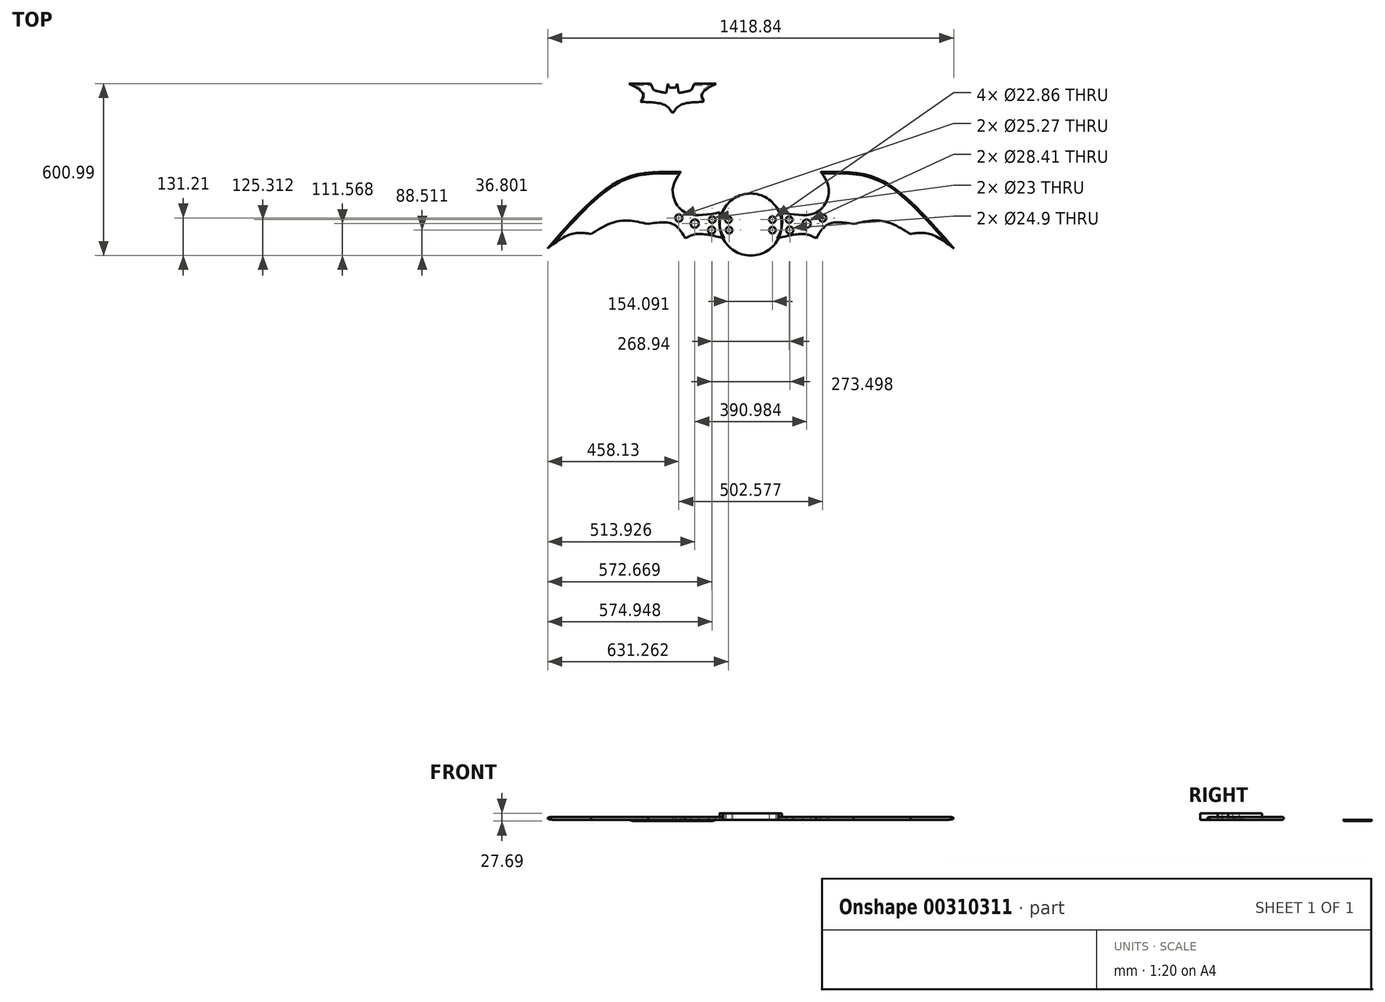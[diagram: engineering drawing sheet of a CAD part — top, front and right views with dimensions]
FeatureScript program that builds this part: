
annotation { "Feature Type Name" : "Feature", "Feature Type Description" : "" }
export const myFeature = defineFeature(function(context is Context, id is Id, definition is map)
    precondition{}
    {
        {
            var Q0;
            Q0=qCreatedBy(makeId("Top.planeOp"),FACE);
            var sketch = newSketch(context, id + "F0", { "sketchPlane" : qUnion([Q0])});
            skLineSegment(sketch, "E0", {"start": v(76.2, 30.48) * mm, "end": v(152.4, 30.48) * mm});
            skLineSegment(sketch, "E1", {"start": v(-76.54, 30.48) * mm, "end": v(-152.74, 30.48) * mm});
            skLineSegment(sketch, "E2", {"start": v(76.2, 30.48) * mm, "end": v(66.04, 7.62) * mm});
            skLineSegment(sketch, "E3", {"start": v(-76.54, 30.48) * mm, "end": v(-66.04, 7.62) * mm});
            skArc(sketch, "E4", {"start": v(-66.04, 7.62) * mm, "mid": v(0, -3.16) * mm, "end": v(66.04, 7.62) * mm});
            skLineSegment(sketch, "E5", {"start": v(21.6, -2.04) * mm, "end": v(16.51, 29.5) * mm});
            skLineSegment(sketch, "E6", {"start": v(16.51, 29.5) * mm, "end": v(11.43, 16.54) * mm});
            skLineSegment(sketch, "E7", {"start": v(11.43, 16.54) * mm, "end": v(-11.43, 16.54) * mm});
            skLineSegment(sketch, "E8", {"start": v(-11.43, 16.54) * mm, "end": v(-16.51, 29.5) * mm});
            skLineSegment(sketch, "E9", {"start": v(-16.51, 29.5) * mm, "end": v(-21.6, -2.04) * mm});
            skPoint(sketch, "E10", {"position": v(0, -76.19) * mm});
            skPoint(sketch, "E11", {"position": v(111.76, -33.5) * mm});
            skPoint(sketch, "E12", {"position": v(-112.1, -33.5) * mm});
            skPoint(sketch, "E13", {"position": v(103.12, -6.18) * mm});
            skPoint(sketch, "E14", {"position": v(-103.47, -6.18) * mm});
            skFitSpline(sketch, "E15", {"points": [v(152.4, 30.48) * mm, v(103.12, -6.18) * mm, v(111.76, -33.5) * mm], "startDerivative": vector(-113.89, -60.03) * mm, "endDerivative": vector(42.43, -68.44) * mm});
            skFitSpline(sketch, "E16", {"points": [v(-152.74, 30.48) * mm, v(-103.47, -6.18) * mm, v(-112.1, -33.5) * mm], "startDerivative": vector(113.89, -60.03) * mm, "endDerivative": vector(-42.43, -68.44) * mm});
            skPoint(sketch, "E17", {"position": v(25.4, -45.7) * mm});
            skPoint(sketch, "E18", {"position": v(-25.4, -45.7) * mm});
            skFitSpline(sketch, "E19", {"points": [v(111.76, -33.5) * mm, v(25.4, -45.7) * mm, v(0, -76.19) * mm], "startDerivative": vector(-168.96, -3.97) * mm, "endDerivative": vector(-46.64, -86.8) * mm});
            skFitSpline(sketch, "E20", {"points": [v(0, -76.19) * mm, v(-25.4, -45.7) * mm, v(-112.1, -33.5) * mm], "startDerivative": vector(-46.65, 86.89) * mm, "endDerivative": vector(-169.55, 3.91) * mm});
            skCircle(sketch, "E21", {"center": v(267.45, 43.06) * mm, "radius": 55.12 * mm});
            skCircle(sketch, "E22", {"center": v(267.45, 43.06) * mm, "radius": 18.05 * mm});
            skPoint(sketch, "E23", {"position": v(238.66, 34.65) * mm});
            skSolve(sketch);
        }
        {
            var Q0;
            {var subQ0=sQuery(id+"F0.wireOp",EDGE,"E5");Q0=makeQuery(id+"F0.imprint","IMPRINT",FACE,{"disambiguationData":[TD([[makeQuery(id+"F0.imprint","IMPRINT",EDGE,{"derivedFrom":subQ0}),1.0]])]});}
            var Q1;
            Q1=makeQuery(id+"F0.imprint","IMPRINT",FACE,{"disambiguationData":[TD([[makeQuery(id+"F0.imprint","IMPRINT",EDGE,{"derivedFrom":sQuery(id+"F0.wireOp",EDGE,"E0")}),-1.0]])]});
            extrude(context, id + "F1", {"entities" : qUnion([Q0, Q1]), "depth" : 4.83 * mm});
        }
        {
            var Q0;
            Q0=makeQuery(id+"F1.opExtrude","CAP_EDGE",EDGE,{"disambiguationData":[OSD([sQuery(id+"F0.wireOp",EDGE,"E0")])],"isStart":true});
            var Q1;
            Q1=makeQuery(id+"F1.opExtrude","CAP_EDGE",EDGE,{"disambiguationData":[OSD([sQuery(id+"F0.wireOp",EDGE,"E1")])],"isStart":true});
            chamfer(context, id + "F2", {"entities" : qUnion([Q0, Q1]), "width" : 5.08 * mm, "tangentPropagation" : true});
        }
        {
            var Q0;
            Q0=makeQuery(id+"F4cRak0Dj6b8y78_0.opExtrude","CAP_EDGE",EDGE,{"disambiguationData":[OSD([sQuery(id+"F0.wireOp",EDGE,"E15")])],"isStart":false});
            var Q1;
            Q1=makeQuery(id+"F1.opExtrude","CAP_EDGE",EDGE,{"disambiguationData":[OSD([sQuery(id+"F0.wireOp",EDGE,"E15")])],"isStart":true});
            var Q2;
            Q2=makeQuery(id+"F1.opExtrude","CAP_EDGE",EDGE,{"disambiguationData":[OSD([sQuery(id+"F0.wireOp",EDGE,"E16")])],"isStart":true});
            var Q3;
            Q3=makeQuery(id+"F1.opExtrude","CAP_EDGE",EDGE,{"disambiguationData":[OSD([sQuery(id+"F0.wireOp",EDGE,"E20")])],"isStart":true});
            fillet(context, id + "F3", {"entities" : qUnion([Q0, Q1, Q2, Q3]), "radius" : 5.08 * mm, "tangentPropagation" : true, "allowEdgeOverflow" : false});
        }
        {
            var Q0;
            Q0=makeQuery(id+"F1.opExtrude","CAP_EDGE",EDGE,{"disambiguationData":[OSD([sQuery(id+"F0.wireOp",EDGE,"E19")])],"isStart":true});
            fillet(context, id + "F4", {"entities" : qUnion([Q0]), "radius" : 5.08 * mm, "tangentPropagation" : true, "allowEdgeOverflow" : false});
        }
        {
            var Q0;
            Q0=makeQuery(id+"F1.opExtrude","CAP_FACE",FACE,{"disambiguationData":[OSD([sQuery(id+"F0.wireOp",EDGE,"E0"),sQuery(id+"F0.wireOp",EDGE,"E1"),sQuery(id+"F0.wireOp",EDGE,"E2"),sQuery(id+"F0.wireOp",EDGE,"E3"),sQuery(id+"F0.wireOp",EDGE,"E4"),sQuery(id+"F0.wireOp",EDGE,"E5"),sQuery(id+"F0.wireOp",EDGE,"E6"),sQuery(id+"F0.wireOp",EDGE,"E7"),sQuery(id+"F0.wireOp",EDGE,"E8"),sQuery(id+"F0.wireOp",EDGE,"E9"),sQuery(id+"F0.wireOp",EDGE,"E15"),sQuery(id+"F0.wireOp",EDGE,"E16"),sQuery(id+"F0.wireOp",EDGE,"E19"),sQuery(id+"F0.wireOp",EDGE,"E20")])],"isStart":false});
            var sketch = newSketch(context, id + "F5", { "sketchPlane" : qUnion([Q0])});
            skPoint(sketch, "E24", {"position": v(165, -419.94) * mm});
            skPoint(sketch, "E25", {"position": v(40.8, -418.85) * mm});
            skPoint(sketch, "E26", {"position": v(-436.54, -545.29) * mm});
            skPoint(sketch, "E27", {"position": v(-288.46, -294.67) * mm});
            skPoint(sketch, "E28", {"position": v(-285.43, -495.15) * mm});
            skPoint(sketch, "E29", {"position": v(-85.93, -460.4) * mm});
            skPoint(sketch, "E30", {"position": v(0, -460.4) * mm});
            skPoint(sketch, "E31", {"position": v(44.27, -510.74) * mm});
            skPoint(sketch, "E32", {"position": v(181.25, -510.74) * mm});
            skPoint(sketch, "E33", {"position": v(165, -472.65) * mm});
            skFitSpline(sketch, "E34", {"points": [v(-436.54, -545.29) * mm, v(-351.75, -495.15) * mm, v(-285.43, -495.15) * mm], "startDerivative": vector(156.35, 116.35) * mm, "endDerivative": vector(145.52, -20.57) * mm});
            skFitSpline(sketch, "E35", {"points": [v(-285.43, -495.15) * mm, v(-188.13, -450.45) * mm, v(-85.93, -460.4) * mm], "startDerivative": vector(189.04, 115.89) * mm, "endDerivative": vector(210.02, -46.94) * mm});
            skFitSpline(sketch, "E36", {"points": [v(-85.93, -460.4) * mm, v(0, -460.4) * mm, v(44.27, -510.74) * mm], "startDerivative": vector(179.75, 28.5) * mm, "endDerivative": vector(78.57, -132.53) * mm});
            skFitSpline(sketch, "E37", {"points": [v(44.27, -510.74) * mm, v(84.17, -495.95) * mm, v(181.25, -510.74) * mm], "startDerivative": vector(88.52, 49.53) * mm, "endDerivative": vector(179.22, -43.16) * mm});
            skFitSpline(sketch, "E38", {"points": [v(181.25, -510.74) * mm, v(165, -472.65) * mm, v(165, -419.94) * mm], "startDerivative": vector(-42.7, 76.75) * mm, "endDerivative": vector(9.16, 104.3) * mm});
            skFitSpline(sketch, "E39", {"points": [v(165, -419.94) * mm, v(40.8, -418.85) * mm, v(0, -343.22) * mm, v(27.76, -278.73) * mm], "startDerivative": vector(-360.34, -65.55) * mm, "endDerivative": vector(140.32, 204.96) * mm});
            skFitSpline(sketch, "E40", {"points": [v(27.76, -278.73) * mm, v(-41.72, -278.73) * mm, v(-184.34, -308.01) * mm, v(-436.54, -545.29) * mm], "startDerivative": vector(-298.58, 3.35) * mm, "endDerivative": vector(-537.55, -618.1) * mm});
            skCircle(sketch, "E41", {"center": v(21.59, -439.55) * mm, "radius": 12.63 * mm});
            skCircle(sketch, "E42", {"center": v(77.39, -459.2) * mm, "radius": 14.2 * mm});
            skCircle(sketch, "E43", {"center": v(138.4, -445.45) * mm, "radius": 11.5 * mm});
            skCircle(sketch, "E44", {"center": v(136.13, -482.25) * mm, "radius": 12.45 * mm});
            skLineSegment(sketch, "E45", {"start": v(272.88, -144.76) * mm, "end": v(272.88, -711.38) * mm});
            skFitSpline(sketch, "E46.MirrorCS", {"points": [v(518, -278.73) * mm, v(587.48, -278.73) * mm, v(730.1, -308.01) * mm, v(982.3, -545.29) * mm], "startDerivative": vector(298.58, 3.35) * mm, "endDerivative": vector(537.55, -618.1) * mm});
            skFitSpline(sketch, "E47.MirrorCS", {"points": [v(982.3, -545.29) * mm, v(897.5, -495.15) * mm, v(831.19, -495.15) * mm], "startDerivative": vector(-156.35, 116.35) * mm, "endDerivative": vector(-145.52, -20.57) * mm});
            skFitSpline(sketch, "E48.MirrorCS", {"points": [v(831.19, -495.15) * mm, v(733.9, -450.45) * mm, v(631.7, -460.4) * mm], "startDerivative": vector(-189.04, 115.89) * mm, "endDerivative": vector(-210.02, -46.94) * mm});
            skFitSpline(sketch, "E49.MirrorCS", {"points": [v(631.7, -460.4) * mm, v(545.76, -460.4) * mm, v(501.5, -510.74) * mm], "startDerivative": vector(-179.75, 28.5) * mm, "endDerivative": vector(-78.57, -132.53) * mm});
            skFitSpline(sketch, "E50.MirrorCS", {"points": [v(501.5, -510.74) * mm, v(461.59, -495.95) * mm, v(364.5, -510.74) * mm], "startDerivative": vector(-88.52, 49.53) * mm, "endDerivative": vector(-179.22, -43.16) * mm});
            skFitSpline(sketch, "E51.MirrorCS", {"points": [v(364.5, -510.74) * mm, v(380.75, -472.65) * mm, v(380.75, -419.94) * mm], "startDerivative": vector(42.7, 76.75) * mm, "endDerivative": vector(-9.16, 104.3) * mm});
            skFitSpline(sketch, "E52.MirrorCS", {"points": [v(380.75, -419.94) * mm, v(504.96, -418.85) * mm, v(545.76, -343.22) * mm, v(518, -278.73) * mm], "startDerivative": vector(360.34, -65.55) * mm, "endDerivative": vector(-140.32, 204.96) * mm});
            skCircle(sketch, "E53.MirrorC", {"center": v(524.17, -439.55) * mm, "radius": 12.63 * mm});
            skCircle(sketch, "E54.MirrorC", {"center": v(468.37, -459.2) * mm, "radius": 14.2 * mm});
            skCircle(sketch, "E55.MirrorC", {"center": v(407.35, -445.45) * mm, "radius": 11.5 * mm});
            skCircle(sketch, "E56.MirrorC", {"center": v(409.63, -482.25) * mm, "radius": 12.45 * mm});
            skCircle(sketch, "E57", {"center": v(272.88, -462.4) * mm, "radius": 108.36 * mm});
            skPoint(sketch, "E58", {"position": v(194.72, -445.45) * mm});
            skPoint(sketch, "E59", {"position": v(197.15, -482.25) * mm});
            skPoint(sketch, "E60", {"position": v(348.81, -445.45) * mm});
            skPoint(sketch, "E61", {"position": v(348.81, -482.25) * mm});
            skSolve(sketch);
        }
        {
            var Q0;
            Q0=makeQuery(id+"F5.imprint","IMPRINT",FACE,{"disambiguationData":[TD([[makeQuery(id+"F5.imprint","IMPRINT",EDGE,{"derivedFrom":sQuery(id+"F5.wireOp",EDGE,"E34")}),1.0]])]});
            extrude(context, id + "F6", {"entities" : qUnion([Q0]), "depth" : 10.16 * mm});
        }
        {
            var Q0;
            Q0=makeQuery(id+"F6.opExtrude","CAP_EDGE",EDGE,{"disambiguationData":[OSD([sQuery(id+"F5.wireOp",EDGE,"E40")])],"isStart":false});
            fillet(context, id + "F7", {"entities" : qUnion([Q0]), "radius" : 5.08 * mm, "tangentPropagation" : true, "allowEdgeOverflow" : false});
        }
        {
            var Q0;
            Q0=makeQuery(id+"F6.opExtrude","CAP_EDGE",EDGE,{"disambiguationData":[OSD([sQuery(id+"F5.wireOp",EDGE,"E40")])],"isStart":true});
            fillet(context, id + "F8", {"entities" : qUnion([Q0]), "radius" : 5.08 * mm, "tangentPropagation" : true, "allowEdgeOverflow" : false});
        }
        {
            var Q0;
            Q0=makeQuery(id+"F5.imprint","IMPRINT",FACE,{"disambiguationData":[TD([[makeQuery(id+"F5.imprint","IMPRINT",EDGE,{"derivedFrom":sQuery(id+"F5.wireOp",EDGE,"E46.MirrorCS")}),-1.0]])]});
            extrude(context, id + "F9", {"entities" : qUnion([Q0]), "depth" : 10.16 * mm});
        }
        {
            var Q0;
            Q0=makeQuery(id+"F9.opExtrude","CAP_EDGE",EDGE,{"disambiguationData":[OSD([sQuery(id+"F5.wireOp",EDGE,"E46.MirrorCS")])],"isStart":false});
            fillet(context, id + "F10", {"entities" : qUnion([Q0]), "radius" : 5.08 * mm, "tangentPropagation" : true, "allowEdgeOverflow" : false});
        }
        {
            var Q0;
            Q0=makeQuery(id+"F9.opExtrude","CAP_EDGE",EDGE,{"disambiguationData":[OSD([sQuery(id+"F5.wireOp",EDGE,"E46.MirrorCS")])],"isStart":true});
            fillet(context, id + "F11", {"entities" : qUnion([Q0]), "radius" : 5.08 * mm, "tangentPropagation" : true, "allowEdgeOverflow" : false});
        }
        {
            var Q0;
            {var subQ3=sQuery(id+"F5.wireOp",EDGE,"E38");var subQ5=sQuery(id+"F5.wireOp",EDGE,"E37");var subQ6=makeQuery(id+"F5.imprint","INTERSECT",VERTEX,{"derivedFrom":[subQ5,subQ3]});Q0=makeQuery(id+"F5.imprint","IMPRINT",FACE,{"disambiguationData":[TD([[makeQuery(id+"F5.imprint","IMPRINT",EDGE,{"disambiguationData":[TD([[subQ6,1.0]])],"derivedFrom":subQ5}),-1.0]])]});}
            var Q1;
            {var subQ0=sQuery(id+"F5.wireOp",EDGE,"E57");var subQ1=sQuery(id+"F5.wireOp",EDGE,"E45");var subQ8=makeQuery(id+"F5.imprint","INTERSECT",VERTEX,{"disambiguationData":[OD(0.0)],"derivedFrom":[subQ1,subQ0]});Q1=makeQuery(id+"F5.imprint","IMPRINT",FACE,{"disambiguationData":[TD([[makeQuery(id+"F5.imprint","IMPRINT",EDGE,{"disambiguationData":[TD([[subQ8,-1.0]])],"derivedFrom":subQ1}),1.0]])]});}
            extrude(context, id + "F12", {"entities" : qUnion([Q0, Q1]), "depth" : 22.86 * mm});
        }
        {
            var Q0;
            Q0=sQuery(id+"F5.wireOp",VERTEX,"E59");
            var Q1;
            Q1=sQuery(id+"F5.wireOp",VERTEX,"E60");
            var Q2;
            Q2=sQuery(id+"F5.wireOp",VERTEX,"E61");
            var Q3;
            Q3=sQuery(id+"F5.wireOp",VERTEX,"E58");
            var Q4;
            Q4=makeQuery(id+"F12.opExtrude","SWEPT_BODY",BODY,{"disambiguationData":[OSD([sQuery(id+"F5.wireOp",EDGE,"E37"),sQuery(id+"F5.wireOp",EDGE,"E38"),sQuery(id+"F5.wireOp",EDGE,"E50.MirrorCS"),sQuery(id+"F5.wireOp",EDGE,"E51.MirrorCS"),sQuery(id+"F5.wireOp",EDGE,"E57")])]});
            hole(context, id + "F13", {"style" : HoleStyle.SIMPLE, "endStyle" : HoleEndStyle.THROUGH, "oppositeDirection" : true, "holeDiameter" : 22.86 * mm, "tappedDepth" : 12.7 * mm, "tapClearance" : 3, "locations" : qUnion([Q0, Q1, Q2, Q3]), "scope" : qUnion([Q4])});
        }
    });
